# Revit family: PEL
name_source: partatom
category: Lighting Fixtures
units: mm (PartAtom-declared; Revit-internal decimal feet)

## family parameters
Cut with Voids When Loaded = No
Host = Face
Light Source = Yes
OmniClass Number = 23.80.70.11.14.17
OmniClass Title = Direct/Indirect
Part Type = Normal
Room Calculation Point = No
Round Connector Dimension = Use Diameter
Shared = Yes

## types (2) — shared parameters
Apparent Load = 52 VA
Assembly Code = D5020200
Ceiling Type = Celing Mount
Color Filter = 16777215
Default Elevation = 48"
Description = Peloton™ High Performance High Bay
Dimming Lamp Color Temperature Shift = Incandescent Lamp Curve
Emit Shape Visible in Rendering = No
Emit from Rectangle Width = 13"
Finish = Arctic White
Glass = White Glass
Lamp = LED
Load Classification = Lighting
Manufacturer = Columbia Lighting
Model = PSL
Photometric Web File = generic.ies
Power Factor = 1
Tilt Angle = 90.00°
Type Comments = Lighting Fixture
URL = https://www.currentlighting.com
Voltage = 120 V
Warranty = Five year warranty
Watts = 52 W

## per-type parameters (varying)
| type | Emit from Rectangle Length | Is 14.59 | Is 17.59 | zz Length 2 |
| PEL4 | 46" | No | Yes | 48" |
| PEL2 | 22" | Yes | No | 24" |

## geometry (parser evidence)
native form markers: Blend x2, Sweep x5
no freeform markers — native parametric forms only
